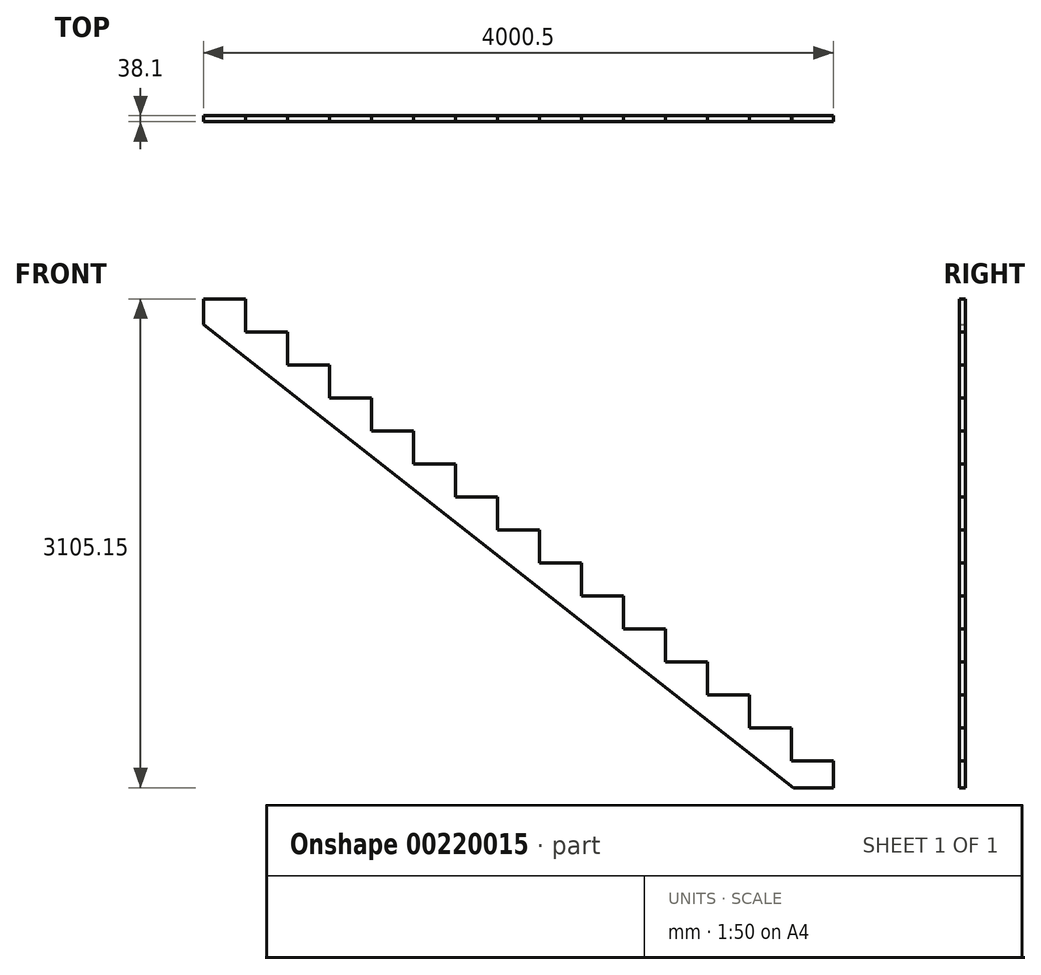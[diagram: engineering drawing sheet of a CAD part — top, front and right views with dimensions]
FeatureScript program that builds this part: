
annotation { "Feature Type Name" : "Feature", "Feature Type Description" : "" }
export const myFeature = defineFeature(function(context is Context, id is Id, definition is map)
    precondition{}
    {
        {
            var Q0;
            Q0=qCreatedBy(makeId("Front.planeOp"),FACE);
            var sketch = newSketch(context, id + "F0", { "sketchPlane" : qUnion([Q0])});
            skLineSegment(sketch, "E0", {"start": v(0, 0) * mm, "end": v(0, 171.45) * mm});
            skLineSegment(sketch, "E1", {"start": v(0, 171.45) * mm, "end": v(-266.7, 171.45) * mm});
            skLineSegment(sketch, "E2", {"start": v(-266.7, 171.45) * mm, "end": v(-266.7, 381) * mm});
            skLineSegment(sketch, "E3", {"start": v(-266.7, 381) * mm, "end": v(-533.4, 381) * mm});
            skLineSegment(sketch, "E4", {"start": v(-533.4, 381) * mm, "end": v(-533.4, 590.55) * mm});
            skLineSegment(sketch, "E5", {"start": v(-533.4, 590.55) * mm, "end": v(-800.1, 590.55) * mm});
            skLineSegment(sketch, "E6", {"start": v(-800.1, 590.55) * mm, "end": v(-800.1, 800.1) * mm});
            skLineSegment(sketch, "E7", {"start": v(-800.1, 800.1) * mm, "end": v(-1066.8, 800.1) * mm});
            skLineSegment(sketch, "E8", {"start": v(-1066.8, 800.1) * mm, "end": v(-1066.8, 1009.65) * mm});
            skLineSegment(sketch, "E9", {"start": v(-1066.8, 1009.65) * mm, "end": v(-1333.5, 1009.65) * mm});
            skLineSegment(sketch, "E10", {"start": v(-1333.5, 1009.65) * mm, "end": v(-1333.5, 1219.2) * mm});
            skLineSegment(sketch, "E11", {"start": v(-1333.5, 1219.2) * mm, "end": v(-1600.2, 1219.2) * mm});
            skLineSegment(sketch, "E12", {"start": v(-1600.2, 1219.2) * mm, "end": v(-1600.2, 1428.75) * mm});
            skLineSegment(sketch, "E13", {"start": v(-1600.2, 1428.75) * mm, "end": v(-1866.9, 1428.75) * mm});
            skLineSegment(sketch, "E14", {"start": v(-1866.9, 1638.3) * mm, "end": v(-2133.6, 1638.3) * mm});
            skLineSegment(sketch, "E15", {"start": v(-2133.6, 1638.3) * mm, "end": v(-2133.6, 1847.85) * mm});
            skLineSegment(sketch, "E16", {"start": v(-2133.6, 1847.85) * mm, "end": v(-2400.3, 1847.85) * mm});
            skLineSegment(sketch, "E17", {"start": v(-2400.3, 1847.85) * mm, "end": v(-2400.3, 2057.4) * mm});
            skLineSegment(sketch, "E18", {"start": v(-2400.3, 2057.4) * mm, "end": v(-2667, 2057.4) * mm});
            skLineSegment(sketch, "E19", {"start": v(-2667, 2057.4) * mm, "end": v(-2667, 2266.95) * mm});
            skLineSegment(sketch, "E20", {"start": v(-2667, 2266.95) * mm, "end": v(-2933.7, 2266.95) * mm});
            skLineSegment(sketch, "E21", {"start": v(-2933.7, 2266.95) * mm, "end": v(-2933.7, 2476.5) * mm});
            skLineSegment(sketch, "E22", {"start": v(-2933.7, 2476.5) * mm, "end": v(-3200.4, 2476.5) * mm});
            skLineSegment(sketch, "E23", {"start": v(-3200.4, 2476.5) * mm, "end": v(-3200.4, 2686.05) * mm});
            skLineSegment(sketch, "E24", {"start": v(-3200.4, 2686.05) * mm, "end": v(-3467.1, 2686.05) * mm});
            skLineSegment(sketch, "E25", {"start": v(-1866.9, 1428.75) * mm, "end": v(-1866.9, 1638.3) * mm});
            skLineSegment(sketch, "E26", {"start": v(-4000.5, 2943.22) * mm, "end": v(-254.58, 0) * mm});
            skLineSegment(sketch, "E27", {"start": v(-254.58, 0) * mm, "end": v(0, 0) * mm});
            skLineSegment(sketch, "E28", {"start": v(-2933.7, 2476.5) * mm, "end": v(-2133.6, 1847.85) * mm, "construction": true});
            skLineSegment(sketch, "E29", {"start": v(-1466.85, 1219.2) * mm, "end": v(-1466.85, 3048) * mm, "construction": true});
            skLineSegment(sketch, "E30", {"start": v(-3467.1, 2686.05) * mm, "end": v(-3467.1, 2895.6) * mm});
            skLineSegment(sketch, "E31", {"start": v(-3467.1, 2895.6) * mm, "end": v(-3733.8, 2895.6) * mm});
            skLineSegment(sketch, "E32", {"start": v(-3733.8, 2895.6) * mm, "end": v(-3733.8, 3105.15) * mm});
            skLineSegment(sketch, "E33", {"start": v(-3733.8, 3105.15) * mm, "end": v(-4000.5, 3105.15) * mm});
            skLineSegment(sketch, "E34", {"start": v(-4000.5, 2943.22) * mm, "end": v(-4000.5, 3105.15) * mm});
            skSolve(sketch);
        }
        {
            var Q0;
            Q0=makeQuery(id+"F0.imprint","IMPRINT",FACE,{"disambiguationData":[TD([[makeQuery(id+"F0.imprint","IMPRINT",EDGE,{"derivedFrom":sQuery(id+"F0.wireOp",EDGE,"E0")}),1.0]])]});
            extrude(context, id + "F1", {"entities" : qUnion([Q0]), "depth" : 38.1 * mm});
        }
    });
